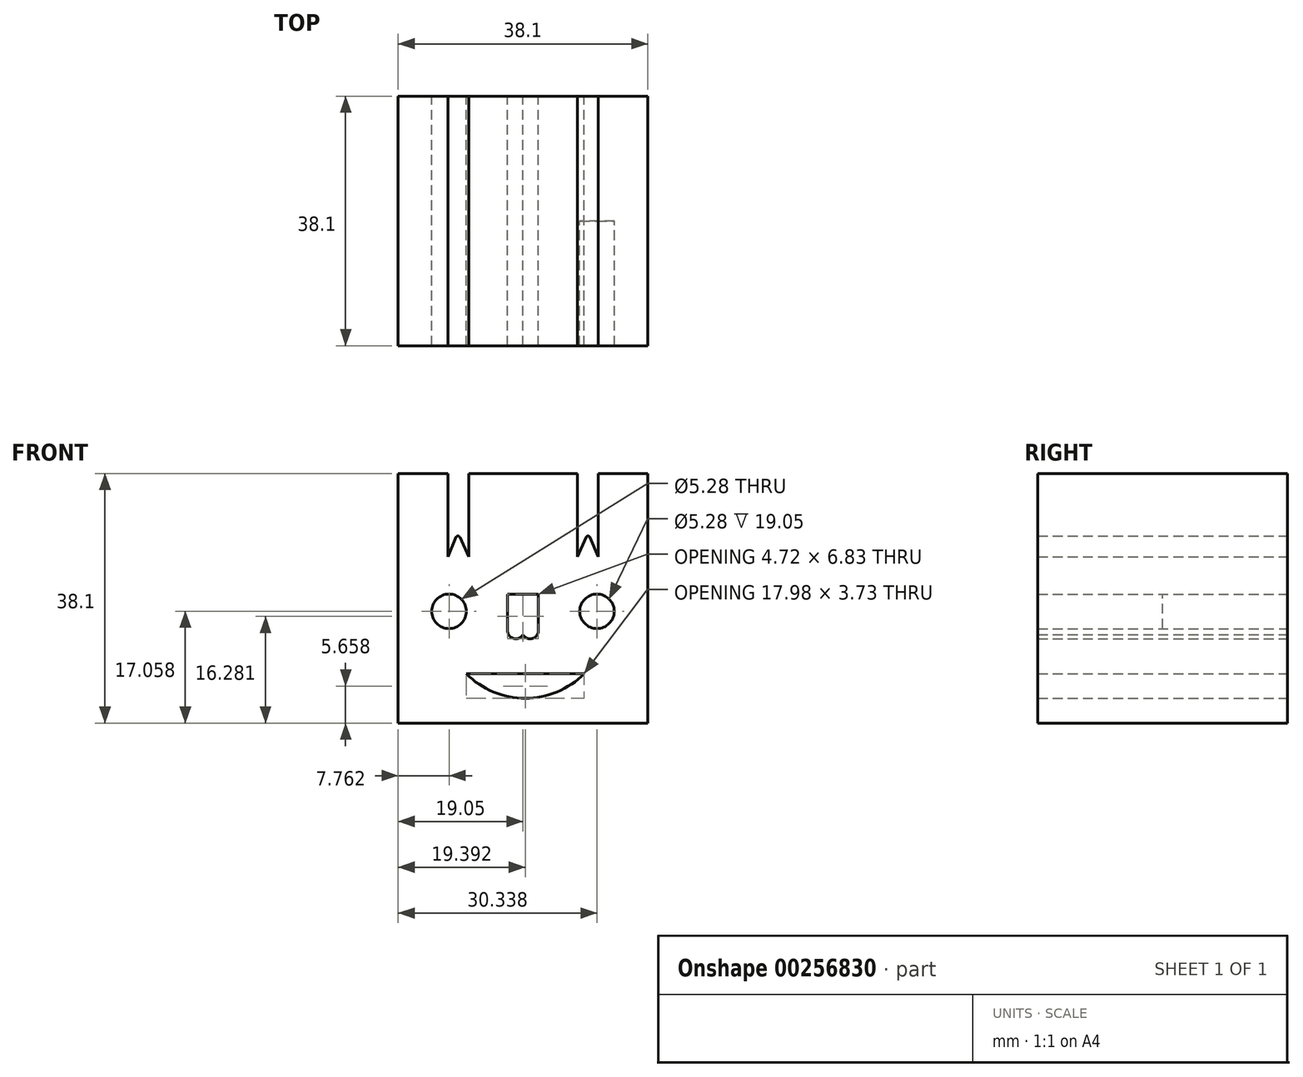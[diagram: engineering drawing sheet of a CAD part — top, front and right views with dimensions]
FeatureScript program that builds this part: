
annotation { "Feature Type Name" : "Feature", "Feature Type Description" : "" }
export const myFeature = defineFeature(function(context is Context, id is Id, definition is map)
    precondition{}
    {
        {
            var Q0;
            Q0=qCreatedBy(makeId("Front.planeOp"),FACE);
            var sketch = newSketch(context, id + "F0", { "sketchPlane" : qUnion([Q0])});
            skLineSegment(sketch, "E0.bottom", {"start": v(-19.05, 19.05) * mm, "end": v(19.05, 19.05) * mm});
            skLineSegment(sketch, "E0.top", {"start": v(-19.05, -19.05) * mm, "end": v(19.05, -19.05) * mm});
            skLineSegment(sketch, "E0.left", {"start": v(-19.05, 19.05) * mm, "end": v(-19.05, -19.05) * mm});
            skLineSegment(sketch, "E0.right", {"start": v(19.05, 19.05) * mm, "end": v(19.05, -19.05) * mm});
            skPoint(sketch, "E0.middle", {"position": v(0, 0) * mm});
            skLineSegment(sketch, "E1", {"start": v(-11.45, 19.05) * mm, "end": v(-11.45, 6.35) * mm});
            skLineSegment(sketch, "E2", {"start": v(-8.3, 19.05) * mm, "end": v(-8.3, 6.35) * mm});
            skLineSegment(sketch, "E3", {"start": v(-11.45, 6.35) * mm, "end": v(-10.23, 9.3) * mm});
            skLineSegment(sketch, "E4", {"start": v(-9.62, 9.3) * mm, "end": v(-8.3, 6.35) * mm});
            skPoint(sketch, "E5.visualSharp", {"position": v(-9.94, 10) * mm});
            skArc(sketch, "E5.filletArc", {"start": v(-9.62, 9.3) * mm, "mid": v(-9.93, 9.5) * mm, "end": v(-10.23, 9.3) * mm});
            skLineSegment(sketch, "E6", {"start": v(0, 19.05) * mm, "end": v(0, 0) * mm});
            skLineSegment(sketch, "E7.MirrorCS", {"start": v(11.45, 19.05) * mm, "end": v(11.45, 6.35) * mm});
            skLineSegment(sketch, "E8.MirrorCS", {"start": v(11.45, 6.35) * mm, "end": v(10.23, 9.3) * mm});
            skLineSegment(sketch, "E9.MirrorCS", {"start": v(9.62, 9.3) * mm, "end": v(8.3, 6.35) * mm});
            skArc(sketch, "E10.MirrorCS", {"start": v(9.62, 9.3) * mm, "mid": v(9.93, 9.5) * mm, "end": v(10.23, 9.3) * mm});
            skLineSegment(sketch, "E11.MirrorCS", {"start": v(8.3, 19.05) * mm, "end": v(8.3, 6.35) * mm});
            skLineSegment(sketch, "E12", {"start": v(-2.36, 0.65) * mm, "end": v(-2.36, -4.92) * mm});
            skLineSegment(sketch, "E13.MirrorCS", {"start": v(2.36, 0.65) * mm, "end": v(2.36, -5.02) * mm});
            skPoint(sketch, "E14.visualSharp", {"position": v(-2.36, -6.33) * mm});
            skArc(sketch, "E14.filletArc", {"start": v(-2.36, -4.92) * mm, "mid": v(-1.43, -6.14) * mm, "end": v(0, -5.57) * mm});
            skPoint(sketch, "E15.visualSharp", {"position": v(2.36, -6.33) * mm});
            skPoint(sketch, "E16.end.orphan", {"position": v(0, -6.33) * mm});
            skPoint(sketch, "E17.visualSharp", {"position": v(0, -5.62) * mm});
            skLineSegment(sketch, "E18.MirrorCS", {"start": v(2.36, 0.65) * mm, "end": v(2.36, -4.92) * mm});
            skArc(sketch, "E19.MirrorCS", {"start": v(2.36, -4.92) * mm, "mid": v(1.43, -6.14) * mm, "end": v(0, -5.57) * mm});
            skLineSegment(sketch, "E20", {"start": v(-8.65, -11.53) * mm, "end": v(9.33, -11.53) * mm});
            skPoint(sketch, "E21", {"position": v(0, -15.25) * mm});
            skArc(sketch, "E22", {"start": v(-8.65, -11.53) * mm, "mid": v(0.34, -15.26) * mm, "end": v(9.33, -11.53) * mm});
            skLineSegment(sketch, "E23", {"start": v(-2.36, 0.65) * mm, "end": v(2.36, 0.65) * mm});
            skCircle(sketch, "E24", {"center": v(11.29, -2) * mm, "radius": 2.64 * mm});
            skCircle(sketch, "E25.MirrorC", {"center": v(-11.29, -2) * mm, "radius": 2.64 * mm});
            skSolve(sketch);
        }
        {
            var Q0;
            Q0=makeQuery(id+"F0.imprint","IMPRINT",FACE,{"disambiguationData":[TD([[makeQuery(id+"F0.imprint","IMPRINT",EDGE,{"derivedFrom":sQuery(id+"F0.wireOp",EDGE,"E0.top")}),1.0]])]});
            extrude(context, id + "F1", {"entities" : qUnion([Q0]), "depth" : 38.1 * mm});
        }
        {
            var Q0;
            Q0=makeQuery(id+"F0.imprint","IMPRINT",FACE,{"disambiguationData":[TD([[makeQuery(id+"F0.imprint","IMPRINT",EDGE,{"derivedFrom":sQuery(id+"F0.wireOp",EDGE,"E25.MirrorC")}),-1.0]])]});
            var Q1;
            Q1=makeQuery(id+"F0.imprint","IMPRINT",FACE,{"disambiguationData":[TD([[makeQuery(id+"F0.imprint","IMPRINT",EDGE,{"derivedFrom":sQuery(id+"F0.wireOp",EDGE,"E24")}),1.0]])]});
            extrude(context, id + "F2", {"entities" : qUnion([Q0, Q1]), "operationType" : NewBodyOperationType.ADD, "depth" : 19.05 * mm});
        }
    });
